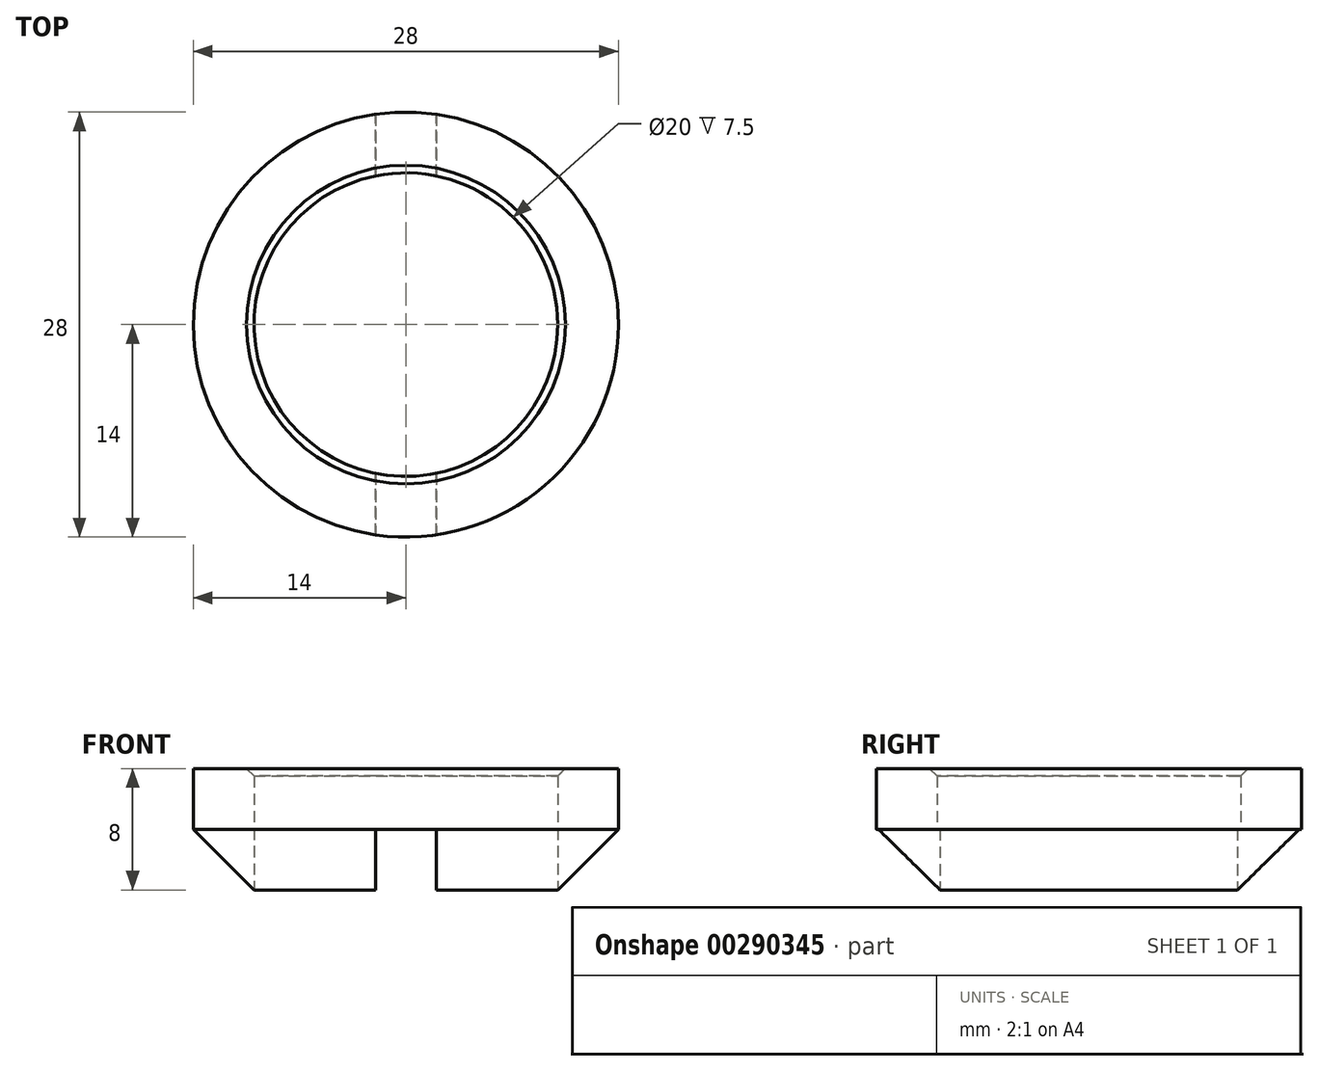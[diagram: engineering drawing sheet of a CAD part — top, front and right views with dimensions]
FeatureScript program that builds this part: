
annotation { "Feature Type Name" : "Feature", "Feature Type Description" : "" }
export const myFeature = defineFeature(function(context is Context, id is Id, definition is map)
    precondition{}
    {
        {
            var Q0;
            Q0=qCreatedBy(makeId("Top.planeOp"),FACE);
            var sketch = newSketch(context, id + "F0", { "sketchPlane" : qUnion([Q0])});
            skCircle(sketch, "E0", {"center": v(0, 0) * mm, "radius": 14 * mm});
            skCircle(sketch, "E1", {"center": v(0, 0) * mm, "radius": 10 * mm});
            skSolve(sketch);
        }
        {
            var Q0;
            Q0 = qSketchRegion(id + "F0", true);
            extrude(context, id + "F1", {"entities" : qUnion([Q0]), "depth" : 4 * mm});
        }
        {
            var Q0;
            Q0=makeQuery(id+"F1.opExtrude","CAP_FACE",FACE,{"disambiguationData":[OSD([sQuery(id+"F0.wireOp",EDGE,"E0"),sQuery(id+"F0.wireOp",EDGE,"E1")])],"isStart":true});
            var sketch = newSketch(context, id + "F2", { "sketchPlane" : qUnion([Q0])});
            skCircle(sketch, "E2", {"center": v(0, 0) * mm, "radius": 10 * mm});
            skCircle(sketch, "E3", {"center": v(0, 0) * mm, "radius": 14 * mm});
            skSolve(sketch);
        }
        {
            var Q0;
            Q0 = qSketchRegion(id + "F2", true);
            extrude(context, id + "F3", {"entities" : qUnion([Q0]), "operationType" : NewBodyOperationType.ADD, "depth" : 4 * mm});
        }
        {
            var Q0;
            Q0=makeQuery(id+"F1.opExtrude","CAP_EDGE",EDGE,{"disambiguationData":[OSD([sQuery(id+"F0.wireOp",EDGE,"E1")])],"isStart":false});
            chamfer(context, id + "F4", {"entities" : qUnion([Q0]), "width" : 0.5 * mm, "tangentPropagation" : true});
        }
        {
            var Q0;
            Q0=makeQuery(id+"F3.opExtrude","CAP_EDGE",EDGE,{"disambiguationData":[OSD([sQuery(id+"F2.wireOp",EDGE,"E3")])],"isStart":false});
            chamfer(context, id + "F5", {"entities" : qUnion([Q0]), "width" : 4 * mm, "tangentPropagation" : true});
        }
        {
            var Q0;
            Q0=qCreatedBy(makeId("Top.planeOp"),FACE);
            var sketch = newSketch(context, id + "F6", { "sketchPlane" : qUnion([Q0])});
            skLineSegment(sketch, "E4.bottom", {"start": v(2, 20) * mm, "end": v(-2, 20) * mm});
            skLineSegment(sketch, "E4.top", {"start": v(2, -20) * mm, "end": v(-2, -20) * mm});
            skLineSegment(sketch, "E4.left", {"start": v(2, 20) * mm, "end": v(2, -20) * mm});
            skLineSegment(sketch, "E4.right", {"start": v(-2, 20) * mm, "end": v(-2, -20) * mm});
            skPoint(sketch, "E4.middle", {"position": v(0, 0) * mm});
            skSolve(sketch);
        }
        {
            var Q0;
            Q0 = qSketchRegion(id + "F6", true);
            extrude(context, id + "F7", {"entities" : qUnion([Q0]), "operationType" : NewBodyOperationType.REMOVE, "endBound" : BoundingType.THROUGH_ALL, "oppositeDirection" : true, "depth" : 25 * mm});
        }
        {
            var Q0;
            Q0=qCreatedBy(makeId("Right.planeOp"),FACE);
            var sketch = newSketch(context, id + "F8", { "sketchPlane" : qUnion([Q0])});
            skLineSegment(sketch, "E5", {"start": v(0, 0) * mm, "end": v(0, 57.95) * mm});
            skSolve(sketch);
        }
    });
